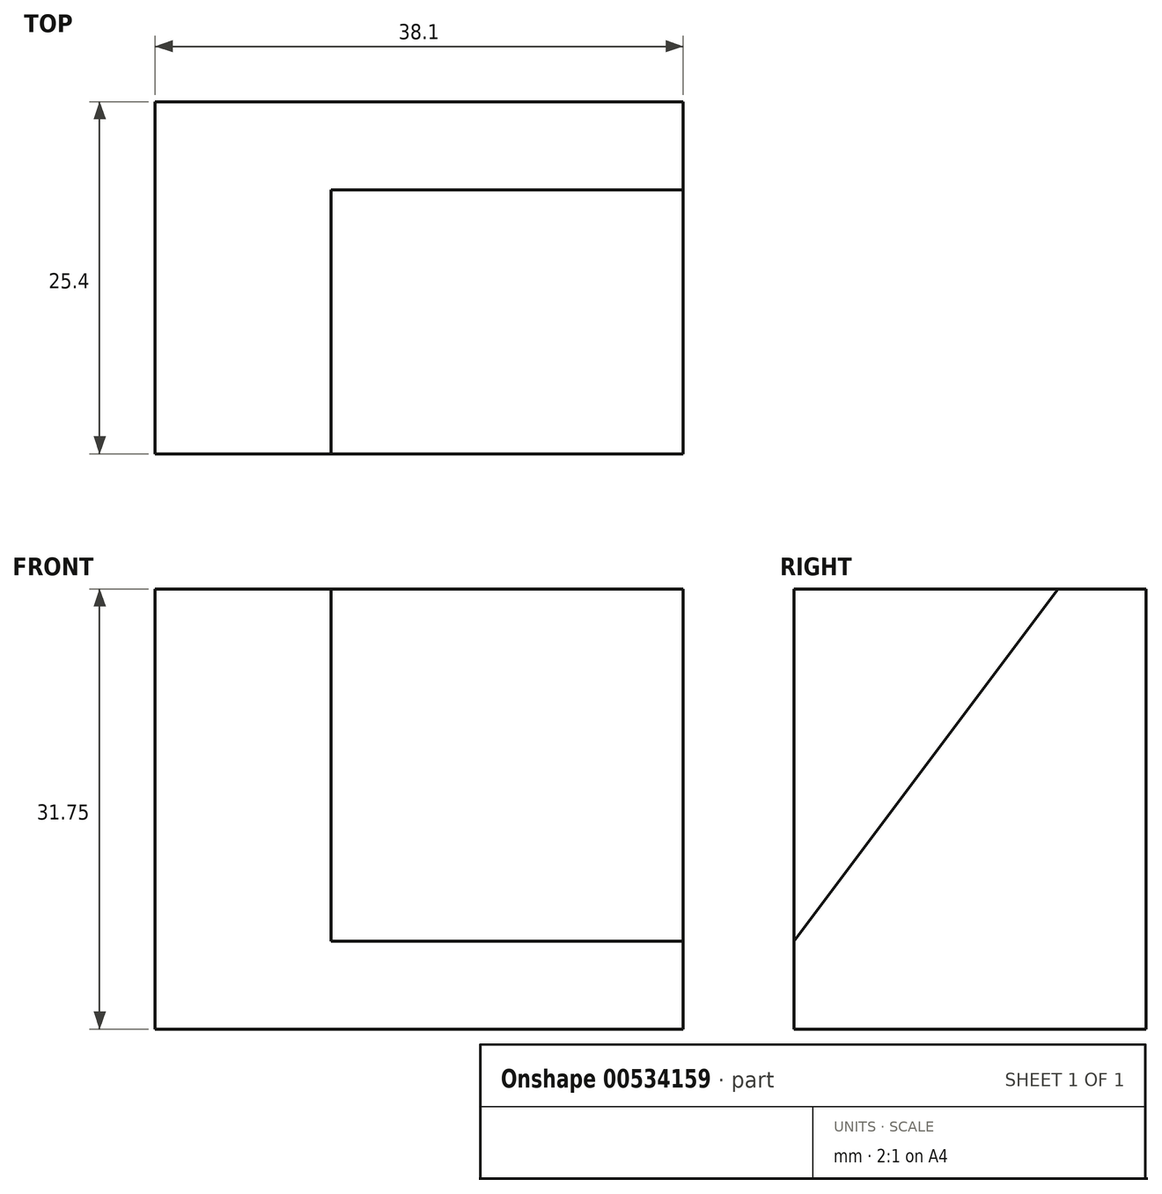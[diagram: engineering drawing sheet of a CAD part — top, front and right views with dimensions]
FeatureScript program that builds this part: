
annotation { "Feature Type Name" : "Feature", "Feature Type Description" : "" }
export const myFeature = defineFeature(function(context is Context, id is Id, definition is map)
    precondition{}
    {
        {
            var Q0;
            Q0=qCreatedBy(makeId("Front.planeOp"),FACE);
            var sketch = newSketch(context, id + "F0", { "sketchPlane" : qUnion([Q0])});
            skLineSegment(sketch, "E0", {"start": v(0, 0) * mm, "end": v(0, 31.75) * mm});
            skLineSegment(sketch, "E1", {"start": v(0, 31.75) * mm, "end": v(38.1, 31.75) * mm});
            skLineSegment(sketch, "E2", {"start": v(38.1, 31.75) * mm, "end": v(38.1, 0) * mm});
            skLineSegment(sketch, "E3", {"start": v(38.1, 0) * mm, "end": v(0, 0) * mm});
            skSolve(sketch);
        }
        {
            var Q0;
            Q0 = qSketchRegion(id + "F0", true);
            extrude(context, id + "F1", {"entities" : qUnion([Q0]), "depth" : 25.4 * mm, "offsetDistance" : 25.4 * mm});
        }
        {
            var Q0;
            Q0=makeQuery(id+"F1.opExtrude","SWEPT_FACE",FACE,{"disambiguationData":[OSD([sQuery(id+"F0.wireOp",EDGE,"E2")])]});
            var sketch = newSketch(context, id + "F2", { "sketchPlane" : qUnion([Q0])});
            skLineSegment(sketch, "E4", {"start": v(-6.35, 31.75) * mm, "end": v(-25.4, 6.35) * mm});
            skSolve(sketch);
        }
        {
            var Q0;
            {var subQ0=sQuery(id+"F2.wireOp",EDGE,"E4");Q0=makeQuery(id+"F2.imprint","IMPRINT",FACE,{"disambiguationData":[TD([[makeQuery(id+"F2.imprint","IMPRINT",EDGE,{"derivedFrom":subQ0}),-1.0]])]});}
            extrude(context, id + "F3", {"entities" : qUnion([Q0]), "operationType" : NewBodyOperationType.REMOVE, "oppositeDirection" : true, "depth" : 25.4 * mm, "offsetDistance" : 25.4 * mm});
        }
    });
